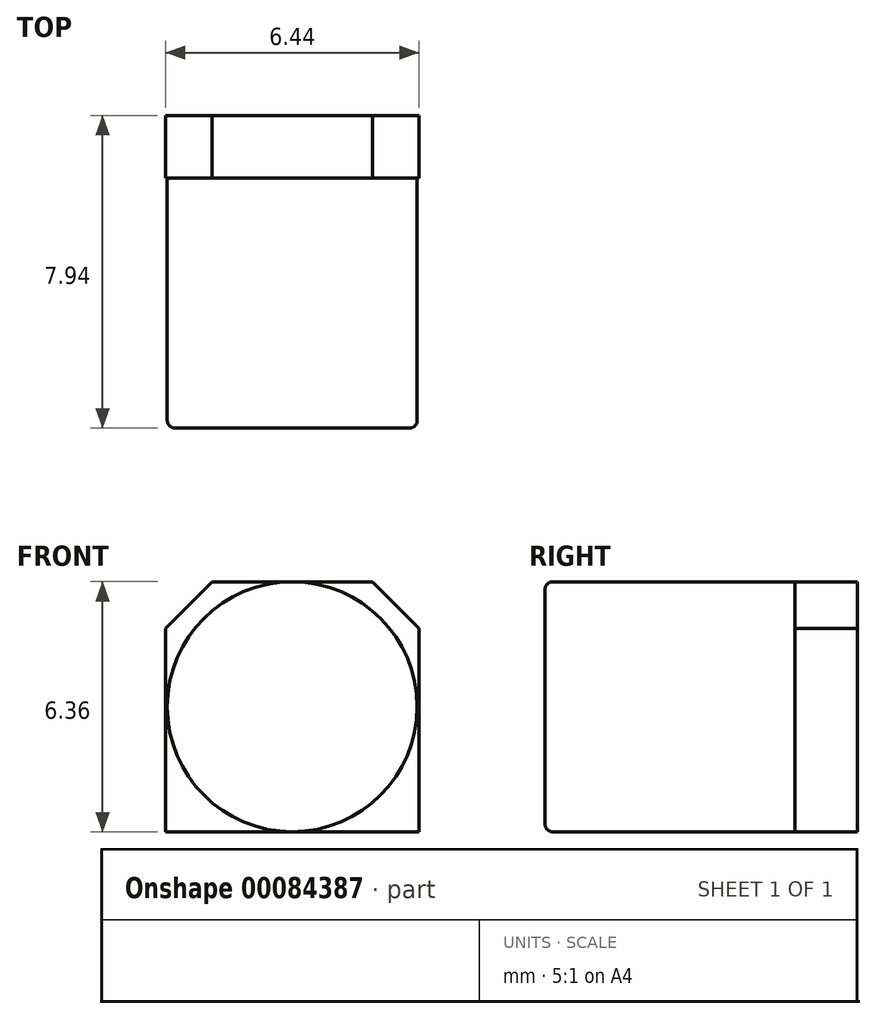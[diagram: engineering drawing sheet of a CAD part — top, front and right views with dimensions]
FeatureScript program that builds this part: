
annotation { "Feature Type Name" : "Feature", "Feature Type Description" : "" }
export const myFeature = defineFeature(function(context is Context, id is Id, definition is map)
    precondition{}
    {
        {
            var Q0;
            Q0=qCreatedBy(makeId("Front.planeOp"),FACE);
            var sketch = newSketch(context, id + "F0", { "sketchPlane" : qUnion([Q0])});
            skCircle(sketch, "E0", {"center": v(0, 0) * mm, "radius": 3.18 * mm});
            skSolve(sketch);
        }
        {
            var Q0;
            Q0 = qSketchRegion(id + "F0", true);
            extrude(context, id + "F1", {"entities" : qUnion([Q0]), "depth" : 6.35 * mm});
        }
        {
            var Q0;
            Q0=makeQuery(id+"F1.opExtrude","CAP_FACE",FACE,{"disambiguationData":[OSD([sQuery(id+"F0.wireOp",EDGE,"E0")])],"isStart":true});
            var sketch = newSketch(context, id + "F2", { "sketchPlane" : qUnion([Q0])});
            skLineSegment(sketch, "E1.bottom", {"start": v(-3.22, 3.18) * mm, "end": v(3.22, 3.18) * mm});
            skLineSegment(sketch, "E1.top", {"start": v(-3.22, -3.18) * mm, "end": v(3.22, -3.18) * mm});
            skLineSegment(sketch, "E1.left", {"start": v(-3.22, 3.18) * mm, "end": v(-3.22, -3.18) * mm});
            skLineSegment(sketch, "E1.right", {"start": v(3.22, 3.18) * mm, "end": v(3.22, -3.17) * mm});
            skPoint(sketch, "E1.middle", {"position": v(0, 0) * mm});
            skLineSegment(sketch, "E2", {"start": v(-3.22, 1.98) * mm, "end": v(-2.03, 3.18) * mm});
            skLineSegment(sketch, "E3", {"start": v(2.03, 3.18) * mm, "end": v(3.22, 1.98) * mm});
            skSolve(sketch);
        }
        {
            var Q0;
            {var subQ3=sQuery(id+"F2.wireOp",EDGE,"E2");Q0=makeQuery(id+"F2.imprint","IMPRINT",FACE,{"disambiguationData":[TD([[makeQuery(id+"F2.imprint","IMPRINT",EDGE,{"derivedFrom":subQ3}),-1.0]])]});}
            var Q1;
            {var subQ5=sQuery(id+"F2.wireOp",EDGE,"E3");Q1=makeQuery(id+"F2.imprint","IMPRINT",FACE,{"disambiguationData":[TD([[makeQuery(id+"F2.imprint","IMPRINT",EDGE,{"derivedFrom":subQ5}),-1.0]])]});}
            var Q2;
            {var subQ0=makeQuery(id+"F1.opExtrude","CAP_EDGE",EDGE,{"disambiguationData":[OSD([sQuery(id+"F0.wireOp",EDGE,"E0")])],"isStart":true});var subQ1=makeQuery(id+"F2.imprint","INTERSECT",VERTEX,{"derivedFrom":[subQ0,sQuery(id+"F2.wireOp",EDGE,"E1.bottom")]});Q2=makeQuery(id+"F2.imprint","IMPRINT",FACE,{"disambiguationData":[TD([[makeQuery(id+"F2.imprint","IMPRINT",EDGE,{"disambiguationData":[TD([[subQ1,1.0]])],"derivedFrom":subQ0}),-1.0]])]});}
            extrude(context, id + "F3", {"entities" : qUnion([Q0, Q1, Q2]), "operationType" : NewBodyOperationType.ADD, "depth" : 1.59 * mm});
        }
        {
            var Q0;
            Q0=makeQuery(id+"F1.opExtrude","CAP_EDGE",EDGE,{"disambiguationData":[OSD([sQuery(id+"F0.wireOp",EDGE,"E0")])],"isStart":false});
            fillet(context, id + "F4", {"entities" : qUnion([Q0]), "radius" : 0.2 * mm, "tangentPropagation" : true, "allowEdgeOverflow" : false});
        }
    });
